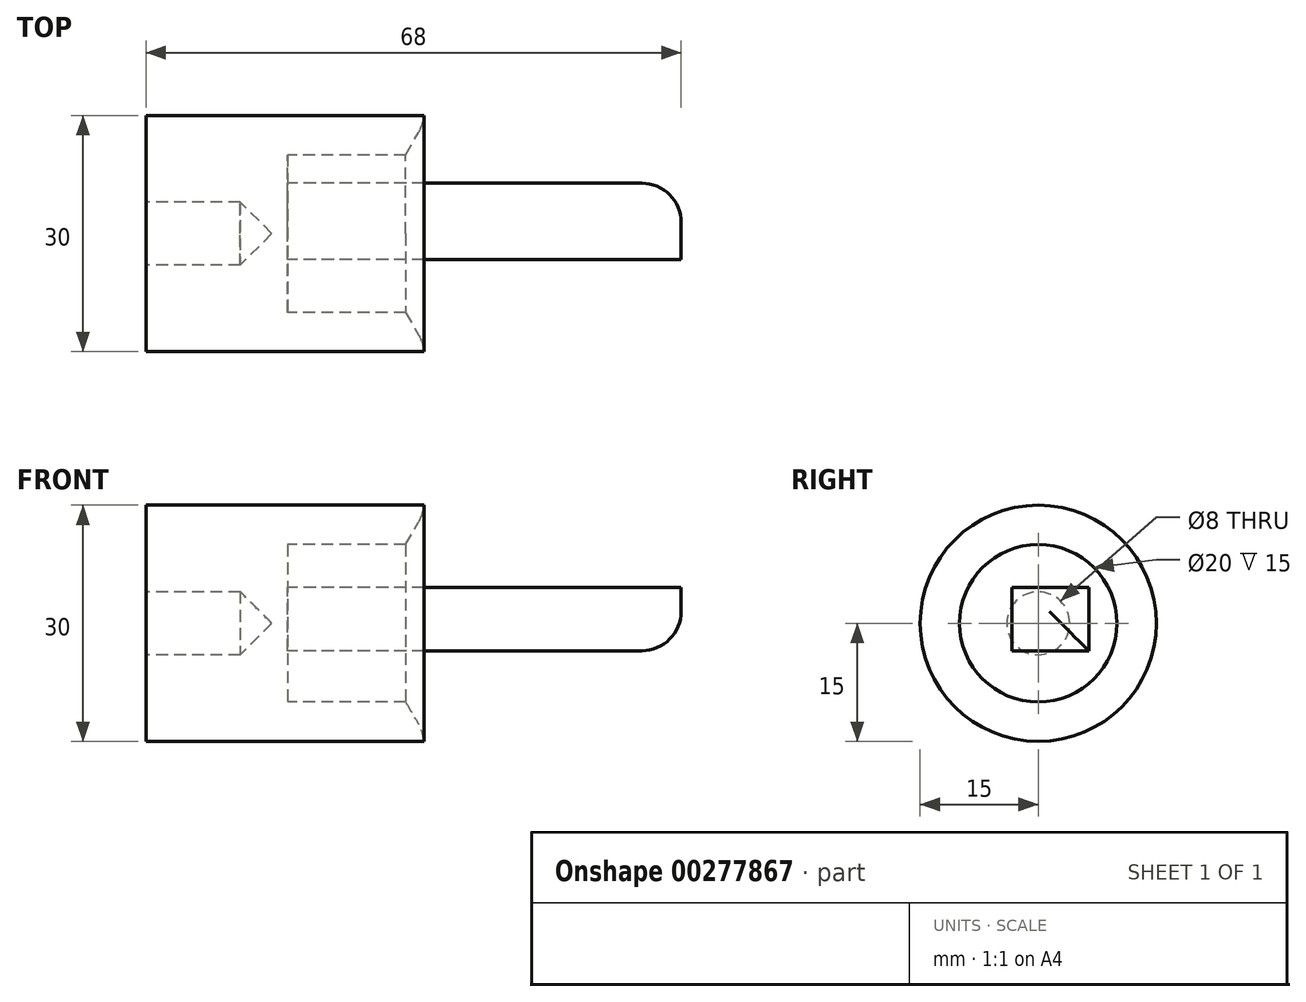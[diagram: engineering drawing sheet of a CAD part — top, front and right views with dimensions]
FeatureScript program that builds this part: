
annotation { "Feature Type Name" : "Feature", "Feature Type Description" : "" }
export const myFeature = defineFeature(function(context is Context, id is Id, definition is map)
    precondition{}
    {
        {
            var Q0;
            Q0=qCreatedBy(makeId("Front.planeOp"),FACE);
            var sketch = newSketch(context, id + "F0", { "sketchPlane" : qUnion([Q0])});
            skLineSegment(sketch, "E0", {"start": v(-4, 4) * mm, "end": v(-16, 4) * mm});
            skLineSegment(sketch, "E1", {"start": v(-16, 4) * mm, "end": v(-16, 15) * mm});
            skLineSegment(sketch, "E2", {"start": v(-16, 15) * mm, "end": v(-13.69, 15) * mm});
            skLineSegment(sketch, "E3", {"start": v(-13.69, 15) * mm, "end": v(19.3, 15) * mm});
            skLineSegment(sketch, "E4", {"start": v(2, 0) * mm, "end": v(0, 0) * mm});
            skLineSegment(sketch, "E5", {"start": v(-19.03, 0) * mm, "end": v(20.32, 0) * mm, "construction": true});
            skLineSegment(sketch, "E6", {"start": v(19.3, 14) * mm, "end": v(17, 10) * mm});
            skLineSegment(sketch, "E7", {"start": v(17, 10) * mm, "end": v(2, 10) * mm});
            skLineSegment(sketch, "E8", {"start": v(2, 10) * mm, "end": v(2, 0) * mm});
            skLineSegment(sketch, "E9", {"start": v(19.3, 14) * mm, "end": v(19.3, 15) * mm});
            skLineSegment(sketch, "E10", {"start": v(-4, 4) * mm, "end": v(0, 0) * mm});
            skSolve(sketch);
        }
        {
            var Q0;
            Q0=makeQuery(id+"F0.imprint","IMPRINT",FACE,{"disambiguationData":[TD([[makeQuery(id+"F0.imprint","IMPRINT",EDGE,{"derivedFrom":sQuery(id+"F0.wireOp",EDGE,"E0")}),-1.0]])]});
            var Q1;
            Q1=sQuery(id+"F0.wireOp",EDGE,"E5");
            revolve(context, id + "F1", {"entities" : qUnion([Q0]), "axis" : qUnion([Q1]), "revolveType" : RevolveType.FULL});
        }
        {
            var Q0;
            Q0=makeQuery(id+"F1.opRevolve","SWEPT_EDGE",EDGE,{"disambiguationData":[OSD([sQuery(id+"F0.wireOp",EDGE,"E6"),sQuery(id+"F0.wireOp",EDGE,"E9")])]});
            fillet(context, id + "F2", {"entities" : qUnion([Q0]), "radius" : 5 * mm, "tangentPropagation" : true, "allowEdgeOverflow" : false});
        }
        {
            var Q0;
            Q0=makeQuery(id+"F1.opRevolve","SWEPT_FACE",FACE,{"disambiguationData":[OSD([sQuery(id+"F0.wireOp",EDGE,"E8")])]});
            var sketch = newSketch(context, id + "F3", { "sketchPlane" : qUnion([Q0])});
            skLineSegment(sketch, "E11.bottom", {"start": v(-3.32, -3.49) * mm, "end": v(6.4, -3.49) * mm});
            skLineSegment(sketch, "E11.top", {"start": v(-3.32, 4.54) * mm, "end": v(6.4, 4.54) * mm});
            skLineSegment(sketch, "E11.left", {"start": v(-3.32, -3.49) * mm, "end": v(-3.32, 4.54) * mm});
            skLineSegment(sketch, "E11.right", {"start": v(6.4, -3.49) * mm, "end": v(6.4, 4.54) * mm});
            skSolve(sketch);
        }
        {
            var Q0;
            Q0=makeQuery(id+"F3.imprint","IMPRINT",FACE,{"disambiguationData":[TD([[makeQuery(id+"F3.imprint","IMPRINT",EDGE,{"derivedFrom":sQuery(id+"F3.wireOp",EDGE,"E11.bottom")}),1.0]])]});
            extrude(context, id + "F4", {"entities" : qUnion([Q0]), "operationType" : NewBodyOperationType.ADD, "depth" : 50 * mm});
        }
        {
            var Q0;
            Q0=makeQuery(id+"F4.opExtrude","CAP_EDGE",EDGE,{"disambiguationData":[OSD([sQuery(id+"F3.wireOp",EDGE,"E11.bottom")])],"isStart":false});
            var Q1;
            Q1=makeQuery(id+"F4.opExtrude","CAP_EDGE",EDGE,{"disambiguationData":[OSD([sQuery(id+"F3.wireOp",EDGE,"E11.right")])],"isStart":false});
            fillet(context, id + "F5", {"entities" : qUnion([Q0, Q1]), "radius" : 5 * mm, "tangentPropagation" : true, "allowEdgeOverflow" : false});
        }
    });
